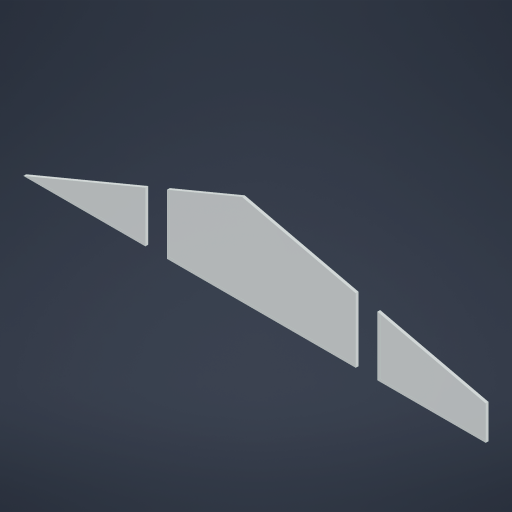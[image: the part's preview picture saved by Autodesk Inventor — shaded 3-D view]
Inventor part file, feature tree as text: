
AUTODESK INVENTOR PART (.ipt)
format: ipt  version: 2023.2 (Build 272271000, 271)  size: 260,096 bytes
history: native  units: mm
features: sketch x1
ambient origin geometry x8: Origin, YZ Plane, XZ Plane, XY Plane, X Axis, Y Axis, Z Axis, Center Point
bodies: Body1 (feature_tree)
feature tree (1):
  sketch  "Sketch1"  dims[d228=105.0deg d268=60.0mm d269=70.0mm d270=300.0mm d273=120.0mm d274=50.0mm d275=105.0deg d283=90.0mm d284=40.0mm d285=45.0mm d289=8.0mm d290=8.0mm d305=2.5mm d306=0.0mm d307=1.5mm d308=0.0mm d9=0.5mm d10=0.872665mm d11=0.5mm d12=0.872665mm d13=0.5mm d14=0.872665mm d27=0.5mm d28=0.872665mm d29=0.5mm d30=0.872665mm d88=0.5mm d89=0.872665mm d90=0.5mm d91=0.872665mm d116=0.5mm d117=0.872665mm d118=0.5mm d119=0.872665mm d154=0.5mm d155=0.872665mm d156=0.5mm d157=0.872665mm d181=0.5mm d182=0.872665mm d183=0.5mm d184=0.872665mm d221=0.5mm d222=0.872665mm d223=0.5mm d224=0.872665mm d301=0.5mm d302=0.872665mm d303=0.5mm d304=0.872665mm]
